# Revit family: T100-PGA-13-FP
name_source: partatom
category: Plumbing Fixtures
revit_build: Autodesk Revit 2018 (Build: 20170223_1515(x64)
units: mm (PartAtom-declared; Revit-internal decimal feet)

## family parameters
Cut with Voids When Loaded = No
Host = Face
Part Type = Normal
Room Calculation Point = No
Round Connector Dimension = Use Radius
Shared = No

## types (2) — shared parameters
Description = Galvanized Steel Perforated Grate to suit 4" clear opening channels
Floor Drain Material = Paint - Sherwin Williams Paint - #952C2A - Bellwood Red
Manufacturer = MIFAB
Sp = 0.5 "
URL = WWW.MIFAB.COM
zero-valued in all types: CWFU, Default Elevation, WFU

## per-type parameters (varying)
| type | L1 | Length | R1 | Visible-1 | Visible-2 |
| T100-PGA-13-FP | 9 " | 39.4 " | 9 " | No | Yes |
| T100-PGA-13-FP-500 | 5 " | 19.7 " | 5 " | Yes | No |

note: column(s) folded — value = type name in every type: Model

## geometry (parser evidence)
native form markers: Sweep x13
no freeform markers — native parametric forms only
